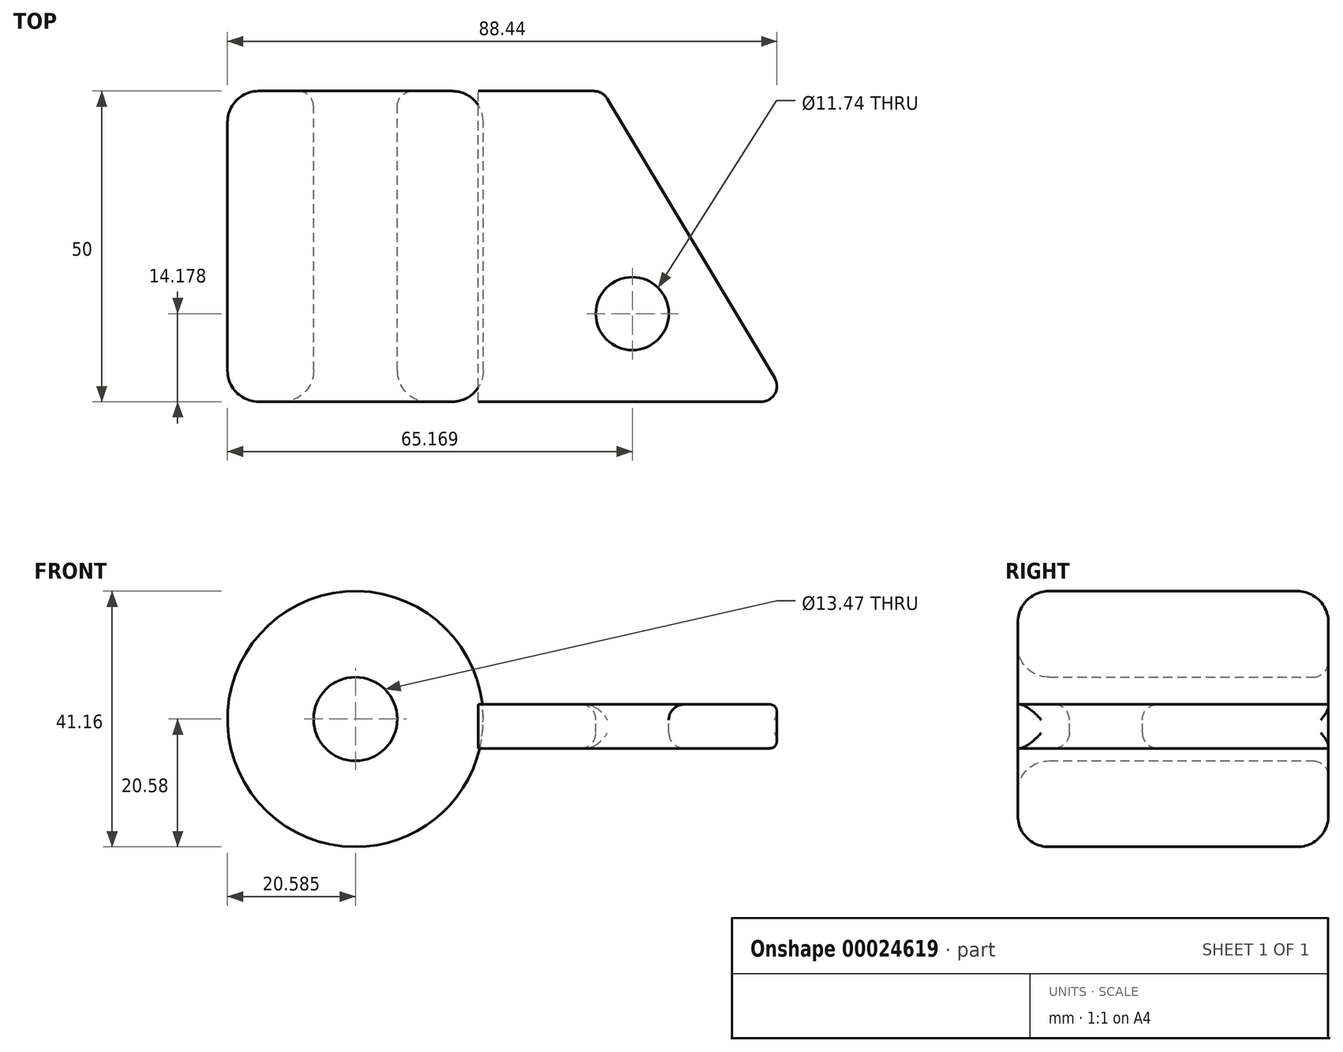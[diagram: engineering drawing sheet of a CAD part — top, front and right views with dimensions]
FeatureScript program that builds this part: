
annotation { "Feature Type Name" : "Feature", "Feature Type Description" : "" }
export const myFeature = defineFeature(function(context is Context, id is Id, definition is map)
    precondition{}
    {
        {
            var Q0;
            Q0=qCreatedBy(makeId("Front.planeOp"),FACE);
            var sketch = newSketch(context, id + "F0", { "sketchPlane" : qUnion([Q0])});
            skCircle(sketch, "E0", {"center": v(-44.76, 6.82) * mm, "radius": 20.58 * mm});
            skCircle(sketch, "E1", {"center": v(-44.76, 6.82) * mm, "radius": 6.74 * mm});
            skSolve(sketch);
        }
        {
            var Q0;
            Q0=makeQuery(id+"F0.imprint","IMPRINT",FACE,{"disambiguationData":[TD([[makeQuery(id+"F0.imprint","IMPRINT",EDGE,{"derivedFrom":sQuery(id+"F0.wireOp",EDGE,"E0")}),1.0]])]});
            extrude(context, id + "F1", {"entities" : qUnion([Q0]), "depth" : 50 * mm});
        }
        {
            var Q0;
            Q0=qCreatedBy(makeId("Right.planeOp"),FACE);
            var sketch = newSketch(context, id + "F2", { "sketchPlane" : qUnion([Q0])});
            skLineSegment(sketch, "E2.bottom", {"start": v(-50.14, 9.18) * mm, "end": v(0, 9.18) * mm});
            skLineSegment(sketch, "E2.top", {"start": v(-50.14, 2.1) * mm, "end": v(0, 2.1) * mm});
            skLineSegment(sketch, "E2.left", {"start": v(-50.14, 9.18) * mm, "end": v(-50.14, 2.1) * mm});
            skLineSegment(sketch, "E2.right", {"start": v(0, 9.18) * mm, "end": v(0, 2.1) * mm});
            skSolve(sketch);
        }
        {
            var Q0;
            Q0=makeQuery(id+"F2.imprint","IMPRINT",FACE,{"disambiguationData":[TD([[makeQuery(id+"F2.imprint","IMPRINT",EDGE,{"derivedFrom":sQuery(id+"F2.wireOp",EDGE,"E2.bottom")}),-1.0]])]});
            extrude(context, id + "F3", {"entities" : qUnion([Q0]), "oppositeDirection" : true, "depth" : 25 * mm});
        }
        {
            var Q0;
            Q0=makeQuery(id+"F3.opExtrude","CAP_FACE",FACE,{"disambiguationData":[OSD([sQuery(id+"F2.wireOp",EDGE,"E2.bottom"),sQuery(id+"F2.wireOp",EDGE,"E2.top"),sQuery(id+"F2.wireOp",EDGE,"E2.left"),sQuery(id+"F2.wireOp",EDGE,"E2.right")])],"isStart":true});
            extrude(context, id + "F4", {"entities" : qUnion([Q0]), "operationType" : NewBodyOperationType.ADD, "depth" : 25 * mm});
        }
        {
            var Q0;
            {var subQ0=sQuery(id+"F2.wireOp",EDGE,"E2.left");Q0=makeQuery(id+"F4.boolean.opBoolean","MERGE",FACE,{"derivedFrom":[makeQuery(id+"F3.opExtrude","SWEPT_FACE",FACE,{"disambiguationData":[OSD([subQ0])]}),makeQuery(id+"F4.opExtrude","SWEPT_FACE",FACE,{"disambiguationData":[OSD([subQ0])]})]});}
            var Q1;
            Q1=makeQuery(id+"F1.opExtrude","CAP_FACE",FACE,{"disambiguationData":[OSD([sQuery(id+"F0.wireOp",EDGE,"E0"),sQuery(id+"F0.wireOp",EDGE,"E1")])],"isStart":false});
            extrude(context, id + "F5", {"entities" : qUnion([Q0]), "operationType" : NewBodyOperationType.REMOVE, "endBound" : BoundingType.UP_TO_SURFACE, "oppositeDirection" : true, "endBoundEntityFace" : qUnion([Q1]), "depth" : 25 * mm});
        }
        {
            var Q0;
            {var subQ0=sQuery(id+"F2.wireOp",EDGE,"E2.bottom");Q0=makeQuery(id+"F4.boolean.opBoolean","MERGE",FACE,{"derivedFrom":[makeQuery(id+"F3.opExtrude","SWEPT_FACE",FACE,{"disambiguationData":[OSD([subQ0])]}),makeQuery(id+"F4.opExtrude","SWEPT_FACE",FACE,{"disambiguationData":[OSD([subQ0])]})]});}
            var sketch = newSketch(context, id + "F6", { "sketchPlane" : qUnion([Q0])});
            skLineSegment(sketch, "E3", {"start": v(25, -50) * mm, "end": v(-4.96, 0) * mm});
            skSolve(sketch);
        }
        {
            var Q0;
            {var subQ3=sQuery(id+"F6.wireOp",EDGE,"E3");Q0=makeQuery(id+"F6.imprint","IMPRINT",FACE,{"disambiguationData":[TD([[makeQuery(id+"F6.imprint","IMPRINT",EDGE,{"derivedFrom":subQ3}),-1.0]])]});}
            extrude(context, id + "F7", {"entities" : qUnion([Q0]), "operationType" : NewBodyOperationType.REMOVE, "endBound" : BoundingType.THROUGH_ALL, "oppositeDirection" : true, "depth" : 25 * mm});
        }
        {
            var Q0;
            {var subQ0=sQuery(id+"F2.wireOp",EDGE,"E2.bottom");Q0=makeQuery(id+"F4.boolean.opBoolean","MERGE",FACE,{"derivedFrom":[makeQuery(id+"F3.opExtrude","SWEPT_FACE",FACE,{"disambiguationData":[OSD([subQ0])]}),makeQuery(id+"F4.opExtrude","SWEPT_FACE",FACE,{"disambiguationData":[OSD([subQ0])]})]});}
            var sketch = newSketch(context, id + "F8", { "sketchPlane" : qUnion([Q0])});
            skCircle(sketch, "E4", {"center": v(-0.18, -35.82) * mm, "radius": 5.87 * mm});
            skSolve(sketch);
        }
        {
            var Q0;
            Q0=makeQuery(id+"F8.imprint","IMPRINT",FACE,{"disambiguationData":[TD([[makeQuery(id+"F8.imprint","IMPRINT",EDGE,{"derivedFrom":sQuery(id+"F8.wireOp",EDGE,"E4")}),1.0]])]});
            extrude(context, id + "F9", {"entities" : qUnion([Q0]), "operationType" : NewBodyOperationType.REMOVE, "endBound" : BoundingType.THROUGH_ALL, "oppositeDirection" : true, "depth" : 25 * mm});
        }
        {
            var Q0;
            Q0=makeQuery(id+"F1.opExtrude","SWEPT_FACE",FACE,{"disambiguationData":[OSD([sQuery(id+"F0.wireOp",EDGE,"E0")])]});
            var Q1;
            Q1=makeQuery(id+"F5.boolean.opBoolean","MERGE",FACE,{"derivedFrom":[makeQuery(id+"F1.opExtrude","CAP_FACE",FACE,{"disambiguationData":[OSD([sQuery(id+"F0.wireOp",EDGE,"E0"),sQuery(id+"F0.wireOp",EDGE,"E1")])],"isStart":false}),makeQuery(id+"F5.opExtrude","CAP_FACE",FACE,{"disambiguationData":[OSD([sQuery(id+"F2.wireOp",EDGE,"E2.left")])],"isStart":false})]});
            fillet(context, id + "F10", {"entities" : qUnion([Q0, Q1]), "radius" : 5 * mm, "tangentPropagation" : true, "allowEdgeOverflow" : false});
        }
        {
            var Q0;
            Q0=makeQuery(id+"F1.opExtrude","SWEPT_FACE",FACE,{"disambiguationData":[OSD([sQuery(id+"F0.wireOp",EDGE,"E0")])]});
            var Q1;
            Q1=makeQuery(id+"F1.opExtrude","SWEPT_FACE",FACE,{"disambiguationData":[OSD([sQuery(id+"F0.wireOp",EDGE,"E1")])]});
            var Q2;
            Q2=makeQuery(id+"F9.boolean.opBoolean","COPY",FACE,{"derivedFrom":makeQuery(id+"F9.opExtrude","SWEPT_FACE",FACE,{"disambiguationData":[OSD([sQuery(id+"F8.wireOp",EDGE,"E4")])]})});
            fillet(context, id + "F11", {"entities" : qUnion([Q0, Q1, Q2]), "radius" : 2.5 * mm, "tangentPropagation" : true, "allowEdgeOverflow" : false});
        }
        {
            var Q0;
            Q0=makeQuery(id+"F7.boolean.opBoolean","COPY",FACE,{"derivedFrom":makeQuery(id+"F7.opExtrude","SWEPT_FACE",FACE,{"disambiguationData":[OSD([sQuery(id+"F6.wireOp",EDGE,"E3")])]})});
            fillet(context, id + "F12", {"entities" : qUnion([Q0]), "radius" : 2.5 * mm, "tangentPropagation" : true, "allowEdgeOverflow" : false});
        }
    });
